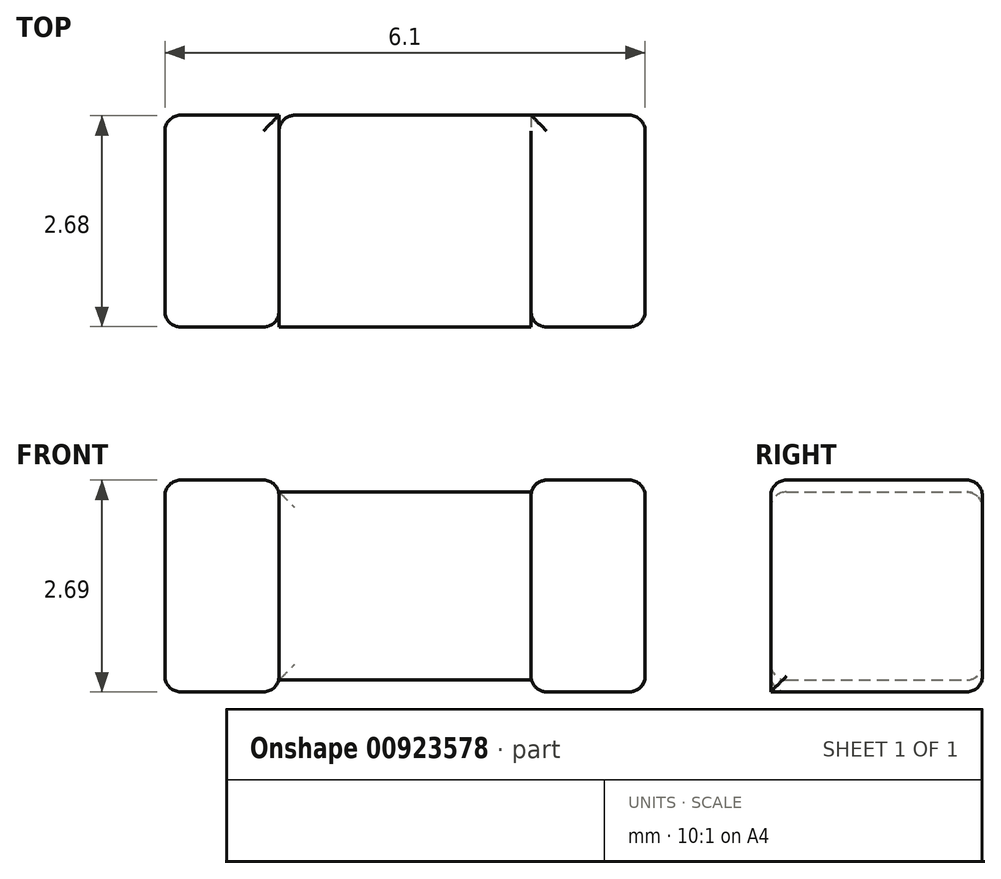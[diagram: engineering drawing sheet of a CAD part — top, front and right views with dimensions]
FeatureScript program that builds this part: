
annotation { "Feature Type Name" : "Feature", "Feature Type Description" : "" }
export const myFeature = defineFeature(function(context is Context, id is Id, definition is map)
    precondition{}
    {
        {
            var Q0;
            Q0=qCreatedBy(makeId("Front.planeOp"),FACE);
            var sketch = newSketch(context, id + "F0", { "sketchPlane" : qUnion([Q0])});
            skLineSegment(sketch, "E0", {"start": v(1.6, 0) * mm, "end": v(3.05, 0) * mm});
            skLineSegment(sketch, "E1", {"start": v(3.05, 0) * mm, "end": v(3.05, 2.69) * mm});
            skLineSegment(sketch, "E2", {"start": v(1.6, 0) * mm, "end": v(1.6, 2.69) * mm});
            skLineSegment(sketch, "E3", {"start": v(1.6, 2.69) * mm, "end": v(1.6, 2.54) * mm});
            skLineSegment(sketch, "E4", {"start": v(1.6, 2.54) * mm, "end": v(0, 2.54) * mm});
            skLineSegment(sketch, "E5", {"start": v(1.6, 0) * mm, "end": v(1.6, 0.15) * mm});
            skLineSegment(sketch, "E6", {"start": v(1.6, 0.15) * mm, "end": v(0, 0.15) * mm});
            skLineSegment(sketch, "E7", {"start": v(1.6, 2.69) * mm, "end": v(3.05, 2.69) * mm});
            skLineSegment(sketch, "E8.MirrorCS", {"start": v(-1.6, 2.69) * mm, "end": v(-3.05, 2.69) * mm});
            skLineSegment(sketch, "E9.MirrorCS", {"start": v(-1.6, 0) * mm, "end": v(-1.6, 0.15) * mm});
            skLineSegment(sketch, "E10.MirrorCS", {"start": v(-1.6, 2.69) * mm, "end": v(-1.6, 2.54) * mm});
            skLineSegment(sketch, "E11.MirrorCS", {"start": v(-1.6, 2.54) * mm, "end": v(0, 2.54) * mm});
            skLineSegment(sketch, "E12.MirrorCS", {"start": v(-1.6, 0) * mm, "end": v(-3.05, 0) * mm});
            skLineSegment(sketch, "E13.MirrorCS", {"start": v(-3.05, 0) * mm, "end": v(-3.05, 2.69) * mm});
            skLineSegment(sketch, "E14.MirrorCS", {"start": v(-1.6, 0) * mm, "end": v(-1.6, 2.69) * mm});
            skLineSegment(sketch, "E15.MirrorCS", {"start": v(-1.6, 0.15) * mm, "end": v(0, 0.15) * mm});
            skSolve(sketch);
        }
        {
            var Q0;
            {var subQ3=sQuery(id+"F0.wireOp",EDGE,"E8.MirrorCS");Q0=makeQuery(id+"F0.imprint","IMPRINT",FACE,{"disambiguationData":[TD([[makeQuery(id+"F0.imprint","IMPRINT",EDGE,{"derivedFrom":subQ3}),1.0]])]});}
            var Q1;
            Q1=makeQuery(id+"F0.imprint","IMPRINT",FACE,{"disambiguationData":[TD([[makeQuery(id+"F0.imprint","IMPRINT",EDGE,{"derivedFrom":sQuery(id+"F0.wireOp",EDGE,"E0")}),1.0]])]});
            extrude(context, id + "F1", {"entities" : qUnion([Q0, Q1]), "endBound" : BoundingType.SYMMETRIC, "depth" : 2.69 * mm, "offsetDistance" : 25 * mm});
        }
        {
            var Q0;
            Q0=makeQuery(id+"F0.imprint","IMPRINT",FACE,{"disambiguationData":[TD([[makeQuery(id+"F0.imprint","IMPRINT",EDGE,{"derivedFrom":sQuery(id+"F0.wireOp",EDGE,"E2")}),1.0]])]});
            extrude(context, id + "F2", {"entities" : qUnion([Q0]), "endBound" : BoundingType.SYMMETRIC, "depth" : 2.69 * mm, "offsetDistance" : 25 * mm});
        }
        {
            var Q0;
            Q0=makeQuery(id+"F1.opExtrude","CAP_EDGE",EDGE,{"disambiguationData":[OSD([sQuery(id+"F0.wireOp",EDGE,"E0")])],"isStart":true});
            var Q1;
            Q1=makeQuery(id+"F1.opExtrude","SWEPT_EDGE",EDGE,{"disambiguationData":[OSD([sQuery(id+"F0.wireOp",EDGE,"E0"),sQuery(id+"F0.wireOp",EDGE,"E1")])]});
            var Q2;
            Q2=makeQuery(id+"F1.opExtrude","CAP_EDGE",EDGE,{"disambiguationData":[OSD([sQuery(id+"F0.wireOp",EDGE,"E1")])],"isStart":false});
            var Q3;
            Q3=makeQuery(id+"F1.opExtrude","SWEPT_EDGE",EDGE,{"disambiguationData":[OSD([sQuery(id+"F0.wireOp",EDGE,"E1"),sQuery(id+"F0.wireOp",EDGE,"E7")])]});
            var Q4;
            Q4=makeQuery(id+"F1.opExtrude","CAP_EDGE",EDGE,{"disambiguationData":[OSD([sQuery(id+"F0.wireOp",EDGE,"E1")])],"isStart":true});
            var Q5;
            Q5=makeQuery(id+"F1.opExtrude","CAP_EDGE",EDGE,{"disambiguationData":[OSD([sQuery(id+"F0.wireOp",EDGE,"E7")])],"isStart":true});
            var Q6;
            Q6=makeQuery(id+"F1.opExtrude","CAP_EDGE",EDGE,{"disambiguationData":[OSD([sQuery(id+"F0.wireOp",EDGE,"E7")])],"isStart":false});
            var Q7;
            Q7=makeQuery(id+"F1.opExtrude","CAP_EDGE",EDGE,{"disambiguationData":[OSD([sQuery(id+"F0.wireOp",EDGE,"E2"),sQuery(id+"F0.wireOp",EDGE,"E3"),sQuery(id+"F0.wireOp",EDGE,"E5")])],"isStart":false});
            var Q8;
            Q8=makeQuery(id+"F1.opExtrude","SWEPT_EDGE",EDGE,{"disambiguationData":[OSD([sQuery(id+"F0.wireOp",EDGE,"E3"),sQuery(id+"F0.wireOp",EDGE,"E7")])]});
            var Q9;
            Q9=makeQuery(id+"F1.opExtrude","SWEPT_EDGE",EDGE,{"disambiguationData":[OSD([sQuery(id+"F0.wireOp",EDGE,"E0"),sQuery(id+"F0.wireOp",EDGE,"E5")])]});
            var Q10;
            Q10=makeQuery(id+"F2.opExtrude","CAP_EDGE",EDGE,{"disambiguationData":[OSD([sQuery(id+"F0.wireOp",EDGE,"E4"),sQuery(id+"F0.wireOp",EDGE,"E11.MirrorCS")])],"isStart":false});
            var Q11;
            Q11=makeQuery(id+"F2.opExtrude","CAP_EDGE",EDGE,{"disambiguationData":[OSD([sQuery(id+"F0.wireOp",EDGE,"E6"),sQuery(id+"F0.wireOp",EDGE,"E15.MirrorCS")])],"isStart":false});
            var Q12;
            Q12=makeQuery(id+"F2.opExtrude","CAP_EDGE",EDGE,{"disambiguationData":[OSD([sQuery(id+"F0.wireOp",EDGE,"E4"),sQuery(id+"F0.wireOp",EDGE,"E11.MirrorCS")])],"isStart":true});
            var Q13;
            Q13=makeQuery(id+"F2.opExtrude","CAP_EDGE",EDGE,{"disambiguationData":[OSD([sQuery(id+"F0.wireOp",EDGE,"E6"),sQuery(id+"F0.wireOp",EDGE,"E15.MirrorCS")])],"isStart":true});
            var Q14;
            Q14=makeQuery(id+"F1.opExtrude","SWEPT_EDGE",EDGE,{"disambiguationData":[OSD([sQuery(id+"F0.wireOp",EDGE,"E12.MirrorCS"),sQuery(id+"F0.wireOp",EDGE,"E13.MirrorCS")])]});
            var Q15;
            Q15=makeQuery(id+"F1.opExtrude","CAP_EDGE",EDGE,{"disambiguationData":[OSD([sQuery(id+"F0.wireOp",EDGE,"E13.MirrorCS")])],"isStart":false});
            var Q16;
            Q16=makeQuery(id+"F1.opExtrude","SWEPT_EDGE",EDGE,{"disambiguationData":[OSD([sQuery(id+"F0.wireOp",EDGE,"E8.MirrorCS"),sQuery(id+"F0.wireOp",EDGE,"E13.MirrorCS")])]});
            var Q17;
            Q17=makeQuery(id+"F1.opExtrude","CAP_EDGE",EDGE,{"disambiguationData":[OSD([sQuery(id+"F0.wireOp",EDGE,"E13.MirrorCS")])],"isStart":true});
            var Q18;
            Q18=makeQuery(id+"F1.opExtrude","CAP_EDGE",EDGE,{"disambiguationData":[OSD([sQuery(id+"F0.wireOp",EDGE,"E12.MirrorCS")])],"isStart":true});
            var Q19;
            Q19=makeQuery(id+"F1.opExtrude","CAP_EDGE",EDGE,{"disambiguationData":[OSD([sQuery(id+"F0.wireOp",EDGE,"E12.MirrorCS")])],"isStart":false});
            var Q20;
            Q20=makeQuery(id+"F1.opExtrude","CAP_EDGE",EDGE,{"disambiguationData":[OSD([sQuery(id+"F0.wireOp",EDGE,"E14.MirrorCS")])],"isStart":false});
            var Q21;
            Q21=makeQuery(id+"F1.opExtrude","SWEPT_EDGE",EDGE,{"disambiguationData":[OSD([sQuery(id+"F0.wireOp",EDGE,"E12.MirrorCS"),sQuery(id+"F0.wireOp",EDGE,"E14.MirrorCS")])]});
            var Q22;
            Q22=makeQuery(id+"F1.opExtrude","CAP_EDGE",EDGE,{"disambiguationData":[OSD([sQuery(id+"F0.wireOp",EDGE,"E8.MirrorCS")])],"isStart":false});
            var Q23;
            Q23=makeQuery(id+"F1.opExtrude","SWEPT_EDGE",EDGE,{"disambiguationData":[OSD([sQuery(id+"F0.wireOp",EDGE,"E8.MirrorCS"),sQuery(id+"F0.wireOp",EDGE,"E14.MirrorCS")])]});
            var Q24;
            Q24=makeQuery(id+"F1.opExtrude","CAP_EDGE",EDGE,{"disambiguationData":[OSD([sQuery(id+"F0.wireOp",EDGE,"E8.MirrorCS")])],"isStart":true});
            var Q25;
            Q25=makeQuery(id+"F2.opExtrude","CAP_EDGE",EDGE,{"disambiguationData":[OSD([sQuery(id+"F0.wireOp",EDGE,"E14.MirrorCS")])],"isStart":true});
            fillet(context, id + "F3", {"entities" : qUnion([Q0, Q1, Q2, Q3, Q4, Q5, Q6, Q7, Q8, Q9, Q10, Q11, Q12, Q13, Q14, Q15, Q16, Q17, Q18, Q19, Q20, Q21, Q22, Q23, Q24, Q25]), "radius" : 0.2 * mm, "tangentPropagation" : true, "allowEdgeOverflow" : false});
        }
    });
